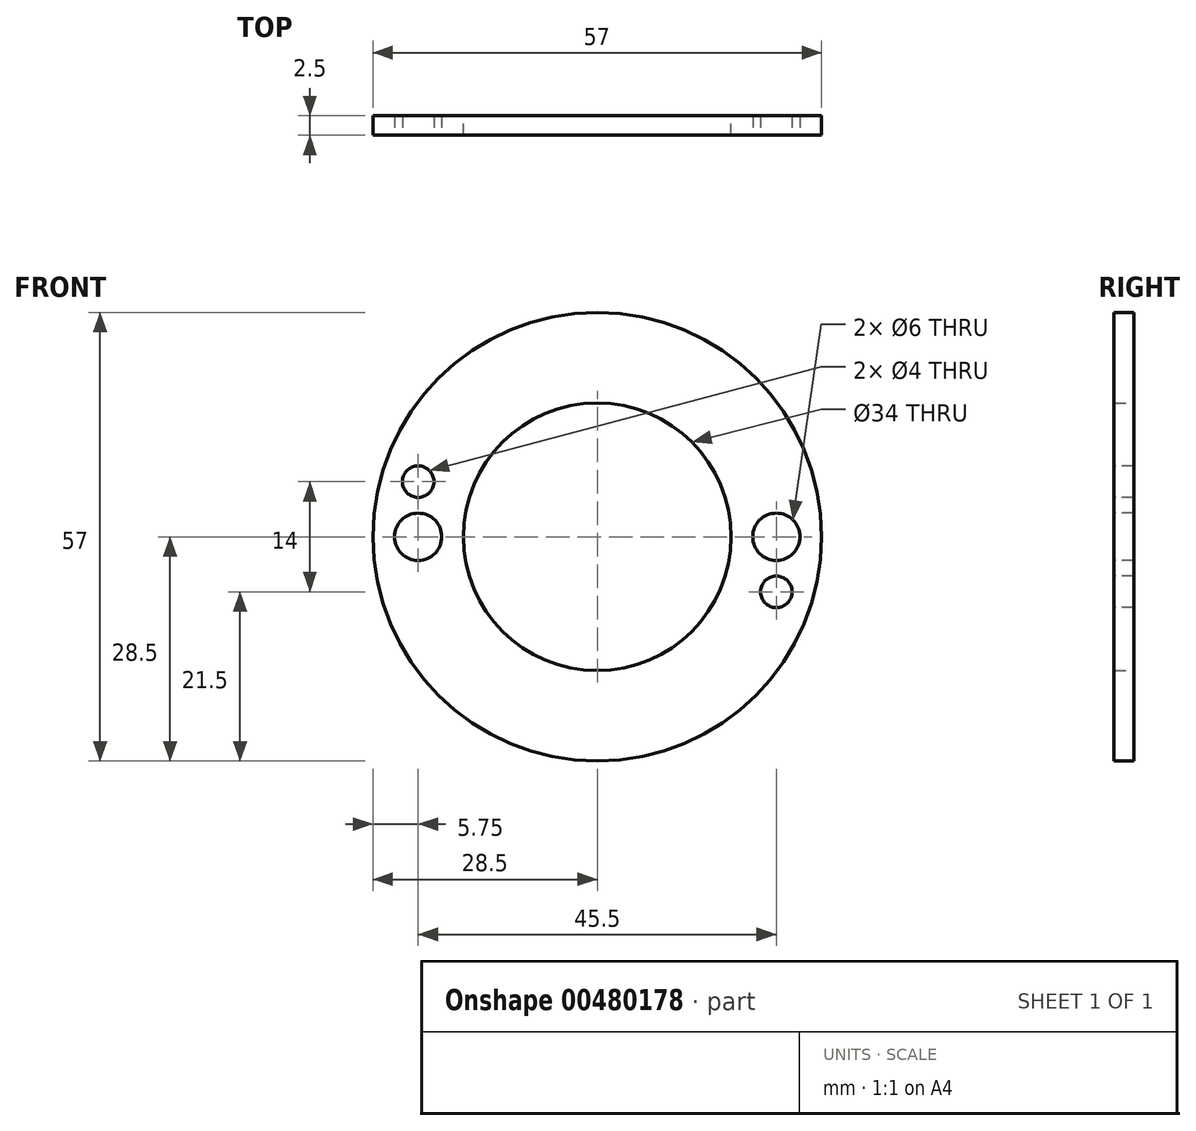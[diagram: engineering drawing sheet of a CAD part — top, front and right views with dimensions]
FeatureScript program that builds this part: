
annotation { "Feature Type Name" : "Feature", "Feature Type Description" : "" }
export const myFeature = defineFeature(function(context is Context, id is Id, definition is map)
    precondition{}
    {
        {
            var Q0;
            Q0=qCreatedBy(makeId("Front.planeOp"),FACE);
            var sketch = newSketch(context, id + "F0", { "sketchPlane" : qUnion([Q0])});
            skCircle(sketch, "E0", {"center": v(0, 0) * mm, "radius": 28.5 * mm});
            skCircle(sketch, "E1", {"center": v(0, 0) * mm, "radius": 17 * mm});
            skSolve(sketch);
        }
        {
            var Q0;
            Q0=makeQuery(id+"F0.imprint","IMPRINT",FACE,{"disambiguationData":[TD([[makeQuery(id+"F0.imprint","IMPRINT",EDGE,{"derivedFrom":sQuery(id+"F0.wireOp",EDGE,"E0")}),1.0]])]});
            extrude(context, id + "F1", {"entities" : qUnion([Q0]), "depth" : 2.5 * mm});
        }
        {
            var Q0;
            Q0=makeQuery(id+"F1.opExtrude","CAP_FACE",FACE,{"disambiguationData":[OSD([sQuery(id+"F0.wireOp",EDGE,"E0"),sQuery(id+"F0.wireOp",EDGE,"E1")])],"isStart":false});
            var sketch = newSketch(context, id + "F2", { "sketchPlane" : qUnion([Q0])});
            skLineSegment(sketch, "E2", {"start": v(-17, 0) * mm, "end": v(-28.5, 0) * mm});
            skLineSegment(sketch, "E3", {"start": v(17, 0) * mm, "end": v(28.5, 0) * mm});
            skCircle(sketch, "E4", {"center": v(-22.75, 0) * mm, "radius": 3 * mm});
            skCircle(sketch, "E5", {"center": v(22.75, 0) * mm, "radius": 3 * mm});
            skSolve(sketch);
        }
        {
            var Q0;
            {var subQ0=sQuery(id+"F2.wireOp",EDGE,"E4");var subQ1=sQuery(id+"F2.wireOp",EDGE,"E2");var subQ2=makeQuery(id+"F2.imprint","INTERSECT",VERTEX,{"disambiguationData":[OD(0.0)],"derivedFrom":[subQ1,subQ0]});Q0=makeQuery(id+"F2.imprint","IMPRINT",FACE,{"disambiguationData":[TD([[makeQuery(id+"F2.imprint","IMPRINT",EDGE,{"disambiguationData":[TD([[subQ2,-1.0]])],"derivedFrom":subQ1}),-1.0]])]});}
            var Q1;
            {var subQ0=sQuery(id+"F2.wireOp",EDGE,"E4");var subQ1=sQuery(id+"F2.wireOp",EDGE,"E2");var subQ2=makeQuery(id+"F2.imprint","INTERSECT",VERTEX,{"disambiguationData":[OD(0.0)],"derivedFrom":[subQ1,subQ0]});Q1=makeQuery(id+"F2.imprint","IMPRINT",FACE,{"disambiguationData":[TD([[makeQuery(id+"F2.imprint","IMPRINT",EDGE,{"disambiguationData":[TD([[subQ2,-1.0]])],"derivedFrom":subQ1}),1.0]])]});}
            var Q2;
            {var subQ0=sQuery(id+"F2.wireOp",EDGE,"E5");var subQ1=sQuery(id+"F2.wireOp",EDGE,"E3");var subQ2=makeQuery(id+"F2.imprint","INTERSECT",VERTEX,{"disambiguationData":[OD(0.0)],"derivedFrom":[subQ1,subQ0]});Q2=makeQuery(id+"F2.imprint","IMPRINT",FACE,{"disambiguationData":[TD([[makeQuery(id+"F2.imprint","IMPRINT",EDGE,{"disambiguationData":[TD([[subQ2,-1.0]])],"derivedFrom":subQ1}),1.0]])]});}
            var Q3;
            {var subQ0=sQuery(id+"F2.wireOp",EDGE,"E5");var subQ1=sQuery(id+"F2.wireOp",EDGE,"E3");var subQ2=makeQuery(id+"F2.imprint","INTERSECT",VERTEX,{"disambiguationData":[OD(0.0)],"derivedFrom":[subQ1,subQ0]});Q3=makeQuery(id+"F2.imprint","IMPRINT",FACE,{"disambiguationData":[TD([[makeQuery(id+"F2.imprint","IMPRINT",EDGE,{"disambiguationData":[TD([[subQ2,-1.0]])],"derivedFrom":subQ1}),-1.0]])]});}
            extrude(context, id + "F3", {"entities" : qUnion([Q0, Q1, Q2, Q3]), "operationType" : NewBodyOperationType.REMOVE, "oppositeDirection" : true, "depth" : 25 * mm});
        }
        {
            var Q0;
            Q0=makeQuery(id+"F1.opExtrude","CAP_FACE",FACE,{"disambiguationData":[OSD([sQuery(id+"F0.wireOp",EDGE,"E0"),sQuery(id+"F0.wireOp",EDGE,"E1")])],"isStart":false});
            var sketch = newSketch(context, id + "F4", { "sketchPlane" : qUnion([Q0])});
            skLineSegment(sketch, "E6", {"start": v(22.75, 0) * mm, "end": v(22.75, -7) * mm});
            skLineSegment(sketch, "E7", {"start": v(22.75, -7) * mm, "end": v(15.5, -7) * mm});
            skLineSegment(sketch, "E8", {"start": v(22.75, -7) * mm, "end": v(27.63, -7) * mm});
            skCircle(sketch, "E9", {"center": v(22.75, -7) * mm, "radius": 2 * mm});
            skSolve(sketch);
        }
        {
            var Q0;
            Q0=makeQuery(id+"F1.opExtrude","CAP_FACE",FACE,{"disambiguationData":[OSD([sQuery(id+"F0.wireOp",EDGE,"E0"),sQuery(id+"F0.wireOp",EDGE,"E1")])],"isStart":false});
            var sketch = newSketch(context, id + "F5", { "sketchPlane" : qUnion([Q0])});
            skLineSegment(sketch, "E10", {"start": v(-22.75, 0) * mm, "end": v(-22.75, 7) * mm});
            skLineSegment(sketch, "E11", {"start": v(-22.75, 7) * mm, "end": v(-15.5, 7) * mm});
            skLineSegment(sketch, "E12", {"start": v(-22.75, 7) * mm, "end": v(-27.63, 7) * mm});
            skCircle(sketch, "E13", {"center": v(-22.75, 7) * mm, "radius": 2 * mm});
            skSolve(sketch);
        }
        {
            var Q0;
            {var subQ1=sQuery(id+"F5.wireOp",EDGE,"E11");var subQ3=sQuery(id+"F5.wireOp",EDGE,"E13");var subQ4=makeQuery(id+"F5.imprint","INTERSECT",VERTEX,{"derivedFrom":[subQ1,subQ3]});Q0=makeQuery(id+"F5.imprint","IMPRINT",FACE,{"disambiguationData":[TD([[makeQuery(id+"F5.imprint","IMPRINT",EDGE,{"disambiguationData":[TD([[subQ4,-1.0]])],"derivedFrom":subQ3}),1.0]])]});}
            var Q1;
            {var subQ1=sQuery(id+"F5.wireOp",EDGE,"E10");var subQ3=sQuery(id+"F5.wireOp",EDGE,"E13");var subQ4=makeQuery(id+"F5.imprint","INTERSECT",VERTEX,{"derivedFrom":[subQ1,subQ3]});Q1=makeQuery(id+"F5.imprint","IMPRINT",FACE,{"disambiguationData":[TD([[makeQuery(id+"F5.imprint","IMPRINT",EDGE,{"disambiguationData":[TD([[subQ4,-1.0]])],"derivedFrom":subQ3}),1.0]])]});}
            var Q2;
            {var subQ1=sQuery(id+"F5.wireOp",EDGE,"E10");var subQ3=sQuery(id+"F5.wireOp",EDGE,"E13");var subQ4=makeQuery(id+"F5.imprint","INTERSECT",VERTEX,{"derivedFrom":[subQ1,subQ3]});Q2=makeQuery(id+"F5.imprint","IMPRINT",FACE,{"disambiguationData":[TD([[makeQuery(id+"F5.imprint","IMPRINT",EDGE,{"disambiguationData":[TD([[subQ4,1.0]])],"derivedFrom":subQ3}),1.0]])]});}
            extrude(context, id + "F6", {"entities" : qUnion([Q0, Q1, Q2]), "operationType" : NewBodyOperationType.REMOVE, "oppositeDirection" : true, "depth" : 25 * mm});
        }
        {
            var Q0;
            {var subQ1=sQuery(id+"F4.wireOp",EDGE,"E7");var subQ3=sQuery(id+"F4.wireOp",EDGE,"E9");var subQ4=makeQuery(id+"F4.imprint","INTERSECT",VERTEX,{"derivedFrom":[subQ1,subQ3]});Q0=makeQuery(id+"F4.imprint","IMPRINT",FACE,{"disambiguationData":[TD([[makeQuery(id+"F4.imprint","IMPRINT",EDGE,{"disambiguationData":[TD([[subQ4,-1.0]])],"derivedFrom":subQ3}),1.0]])]});}
            var Q1;
            {var subQ1=sQuery(id+"F4.wireOp",EDGE,"E6");var subQ3=sQuery(id+"F4.wireOp",EDGE,"E9");var subQ4=makeQuery(id+"F4.imprint","INTERSECT",VERTEX,{"derivedFrom":[subQ1,subQ3]});Q1=makeQuery(id+"F4.imprint","IMPRINT",FACE,{"disambiguationData":[TD([[makeQuery(id+"F4.imprint","IMPRINT",EDGE,{"disambiguationData":[TD([[subQ4,-1.0]])],"derivedFrom":subQ3}),1.0]])]});}
            var Q2;
            {var subQ1=sQuery(id+"F4.wireOp",EDGE,"E6");var subQ3=sQuery(id+"F4.wireOp",EDGE,"E9");var subQ4=makeQuery(id+"F4.imprint","INTERSECT",VERTEX,{"derivedFrom":[subQ1,subQ3]});Q2=makeQuery(id+"F4.imprint","IMPRINT",FACE,{"disambiguationData":[TD([[makeQuery(id+"F4.imprint","IMPRINT",EDGE,{"disambiguationData":[TD([[subQ4,1.0]])],"derivedFrom":subQ3}),1.0]])]});}
            extrude(context, id + "F7", {"entities" : qUnion([Q0, Q1, Q2]), "operationType" : NewBodyOperationType.REMOVE, "oppositeDirection" : true, "depth" : 25 * mm});
        }
    });
